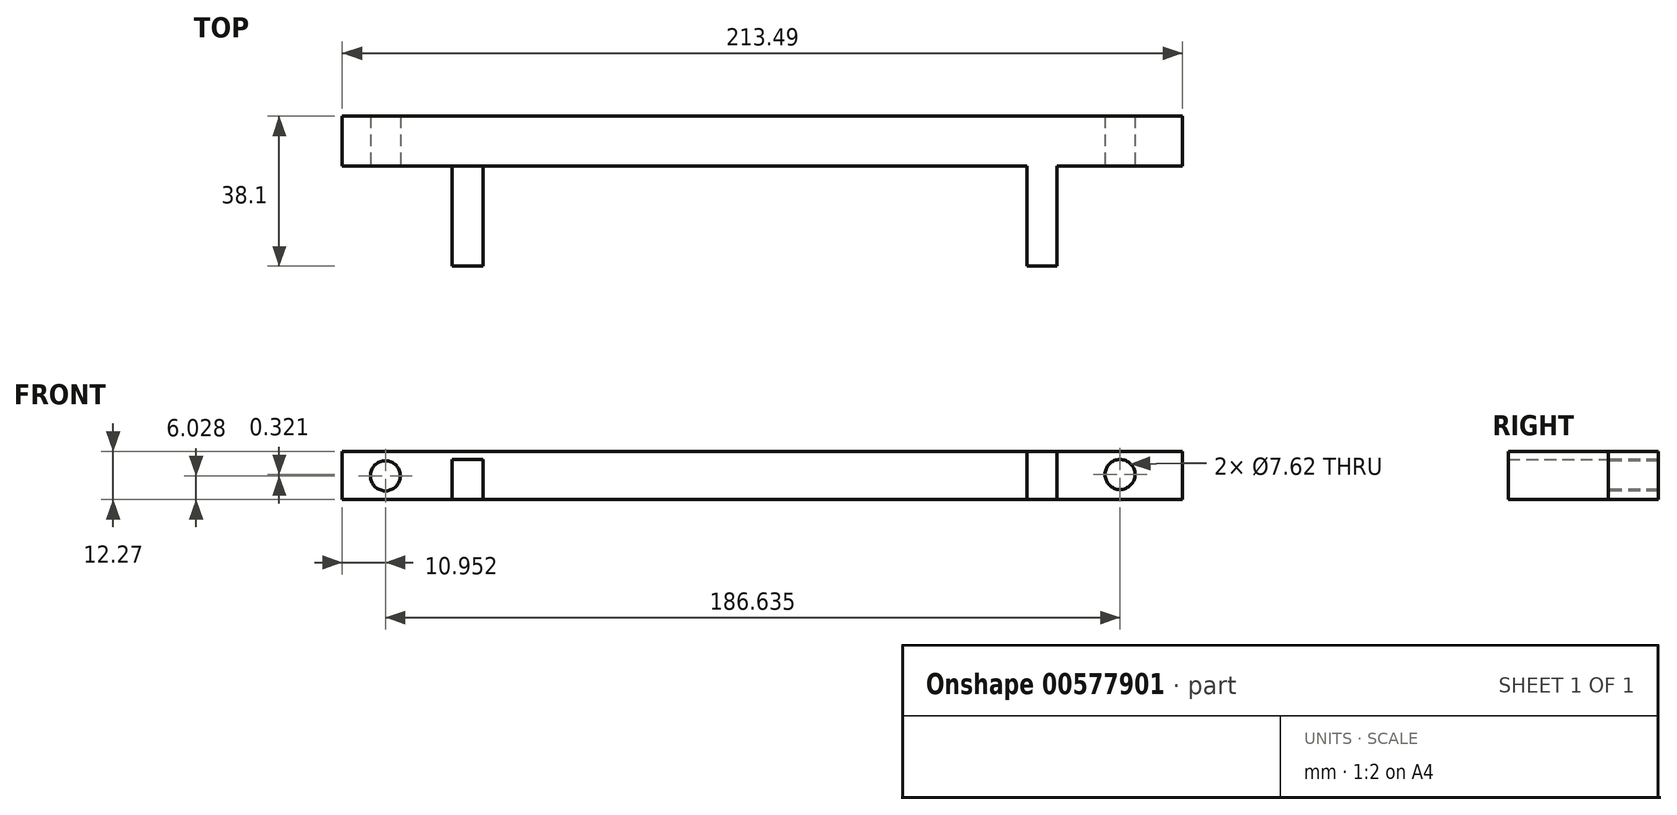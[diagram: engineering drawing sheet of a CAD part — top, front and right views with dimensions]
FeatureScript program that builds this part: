
annotation { "Feature Type Name" : "Feature", "Feature Type Description" : "" }
export const myFeature = defineFeature(function(context is Context, id is Id, definition is map)
    precondition{}
    {
        {
            var Q0;
            Q0=qCreatedBy(makeId("Front.planeOp"),FACE);
            var sketch = newSketch(context, id + "F0", { "sketchPlane" : qUnion([Q0])});
            skLineSegment(sketch, "E0.bottom", {"start": v(-75.05, 47.97) * mm, "end": v(138.44, 47.97) * mm});
            skLineSegment(sketch, "E0.top", {"start": v(-75.05, 35.7) * mm, "end": v(138.44, 35.7) * mm});
            skLineSegment(sketch, "E0.left", {"start": v(-75.05, 47.97) * mm, "end": v(-75.05, 35.7) * mm});
            skLineSegment(sketch, "E0.right", {"start": v(138.44, 47.97) * mm, "end": v(138.44, 35.7) * mm});
            skSolve(sketch);
        }
        {
            var Q0;
            Q0=makeQuery(id+"F0.imprint","IMPRINT",FACE,{"disambiguationData":[TD([[makeQuery(id+"F0.imprint","IMPRINT",EDGE,{"derivedFrom":sQuery(id+"F0.wireOp",EDGE,"E0.bottom")}),-1.0]])]});
            extrude(context, id + "F1", {"entities" : qUnion([Q0]), "depth" : 12.7 * mm, "offsetDistance" : 25.4 * mm});
        }
        {
            var Q0;
            Q0=makeQuery(id+"F1.opExtrude","CAP_FACE",FACE,{"disambiguationData":[OSD([sQuery(id+"F0.wireOp",EDGE,"E0.bottom"),sQuery(id+"F0.wireOp",EDGE,"E0.top"),sQuery(id+"F0.wireOp",EDGE,"E0.left"),sQuery(id+"F0.wireOp",EDGE,"E0.right")])],"isStart":false});
            var sketch = newSketch(context, id + "F2", { "sketchPlane" : qUnion([Q0])});
            skPoint(sketch, "E1", {"position": v(-63.84, 35.7) * mm});
            skPoint(sketch, "E2", {"position": v(-64.1, 41.73) * mm});
            skSolve(sketch);
        }
        {
            var Q0;
            Q0=sQuery(id+"F2.wireOp",VERTEX,"E2");
            var Q1;
            Q1=makeQuery(id+"F1.opExtrude","SWEPT_BODY",BODY,{"disambiguationData":[OSD([sQuery(id+"F0.wireOp",EDGE,"E0.bottom"),sQuery(id+"F0.wireOp",EDGE,"E0.top"),sQuery(id+"F0.wireOp",EDGE,"E0.left"),sQuery(id+"F0.wireOp",EDGE,"E0.right")])]});
            hole(context, id + "F3", {"style" : HoleStyle.SIMPLE, "endStyle" : HoleEndStyle.THROUGH, "holeDiameter" : 7.62 * mm, "isTappedThrough" : true, "tappedDepth" : 12.7 * mm, "tapClearance" : 3, "locations" : qUnion([Q0]), "scope" : qUnion([Q1])});
        }
        {
            var Q0;
            Q0=makeQuery(id+"F1.opExtrude","CAP_FACE",FACE,{"disambiguationData":[OSD([sQuery(id+"F0.wireOp",EDGE,"E0.bottom"),sQuery(id+"F0.wireOp",EDGE,"E0.top"),sQuery(id+"F0.wireOp",EDGE,"E0.left"),sQuery(id+"F0.wireOp",EDGE,"E0.right")])],"isStart":false});
            var sketch = newSketch(context, id + "F4", { "sketchPlane" : qUnion([Q0])});
            skPoint(sketch, "E3", {"position": v(122.54, 35.7) * mm});
            skPoint(sketch, "E4", {"position": v(122.54, 42.05) * mm});
            skSolve(sketch);
        }
        {
            var Q0;
            Q0=sQuery(id+"F4.wireOp",VERTEX,"E4");
            var Q1;
            Q1=makeQuery(id+"F1.opExtrude","SWEPT_BODY",BODY,{"disambiguationData":[OSD([sQuery(id+"F0.wireOp",EDGE,"E0.bottom"),sQuery(id+"F0.wireOp",EDGE,"E0.top"),sQuery(id+"F0.wireOp",EDGE,"E0.left"),sQuery(id+"F0.wireOp",EDGE,"E0.right")])]});
            hole(context, id + "F5", {"style" : HoleStyle.SIMPLE, "endStyle" : HoleEndStyle.THROUGH, "holeDiameter" : 7.62 * mm, "isTappedThrough" : true, "tappedDepth" : 12.7 * mm, "tapClearance" : 3, "locations" : qUnion([Q0]), "scope" : qUnion([Q1])});
        }
        {
            var Q0;
            Q0=qCreatedBy(makeId("Front.planeOp"),FACE);
            var sketch = newSketch(context, id + "F6", { "sketchPlane" : qUnion([Q0])});
            skLineSegment(sketch, "E5", {"start": v(-47.13, 45.94) * mm, "end": v(-47.13, 40.67) * mm});
            skLineSegment(sketch, "E6", {"start": v(-47.13, 40.67) * mm, "end": v(-39.24, 40.67) * mm});
            skLineSegment(sketch, "E7", {"start": v(-39.24, 40.67) * mm, "end": v(-39.24, 45.94) * mm});
            skLineSegment(sketch, "E8", {"start": v(-39.24, 45.94) * mm, "end": v(-47.13, 45.94) * mm});
            skSolve(sketch);
        }
        {
            var Q0;
            Q0=makeQuery(id+"F6.imprint","IMPRINT",FACE,{"disambiguationData":[TD([[makeQuery(id+"F6.imprint","IMPRINT",EDGE,{"derivedFrom":sQuery(id+"F6.wireOp",EDGE,"E5")}),1.0]])]});
            extrude(context, id + "F7", {"entities" : qUnion([Q0]), "operationType" : NewBodyOperationType.ADD, "depth" : 25.4 * mm, "offsetDistance" : 25.4 * mm});
        }
        {
            var Q0;
            Q0=makeQuery(id+"F1.opExtrude","CAP_FACE",FACE,{"disambiguationData":[OSD([sQuery(id+"F0.wireOp",EDGE,"E0.bottom"),sQuery(id+"F0.wireOp",EDGE,"E0.top"),sQuery(id+"F0.wireOp",EDGE,"E0.left"),sQuery(id+"F0.wireOp",EDGE,"E0.right")])],"isStart":false});
            var sketch = newSketch(context, id + "F8", { "sketchPlane" : qUnion([Q0])});
            skLineSegment(sketch, "E9", {"start": v(106.47, 35.7) * mm, "end": v(106.47, 47.97) * mm});
            skLineSegment(sketch, "E10", {"start": v(106.47, 47.97) * mm, "end": v(98.88, 47.97) * mm});
            skLineSegment(sketch, "E11", {"start": v(98.88, 47.97) * mm, "end": v(98.88, 35.7) * mm});
            skLineSegment(sketch, "E12", {"start": v(98.88, 35.7) * mm, "end": v(106.47, 35.7) * mm});
            skSolve(sketch);
        }
        {
            var Q0;
            Q0=makeQuery(id+"F8.imprint","IMPRINT",FACE,{"disambiguationData":[TD([[makeQuery(id+"F8.imprint","IMPRINT",EDGE,{"derivedFrom":sQuery(id+"F8.wireOp",EDGE,"E9")}),1.0]])]});
            extrude(context, id + "F9", {"entities" : qUnion([Q0]), "operationType" : NewBodyOperationType.ADD, "depth" : 25.4 * mm, "offsetDistance" : 25.4 * mm});
        }
        {
            var Q0;
            {var subQ0=sQuery(id+"F0.wireOp",EDGE,"E0.bottom");var subQ1=sQuery(id+"F0.wireOp",EDGE,"E0.top");var subQ2=sQuery(id+"F0.wireOp",EDGE,"E0.left");Q0=makeQuery(id+"F9.boolean.opBoolean","SPLIT",FACE,{"disambiguationData":[TD([makeQuery(id+"F1.opExtrude","SWEPT_FACE",FACE,{"disambiguationData":[OSD([subQ2])]})])],"derivedFrom":makeQuery(id+"F1.opExtrude","CAP_FACE",FACE,{"disambiguationData":[OSD([subQ0,subQ1,subQ2,sQuery(id+"F0.wireOp",EDGE,"E0.right")])],"isStart":false})});}
            var sketch = newSketch(context, id + "F10", { "sketchPlane" : qUnion([Q0])});
            skLineSegment(sketch, "E13", {"start": v(-47.13, 40.67) * mm, "end": v(-47.13, 35.7) * mm});
            skLineSegment(sketch, "E14", {"start": v(-47.13, 35.7) * mm, "end": v(-39.24, 35.7) * mm});
            skLineSegment(sketch, "E15", {"start": v(-39.24, 35.7) * mm, "end": v(-39.24, 40.67) * mm});
            skLineSegment(sketch, "E16", {"start": v(-39.24, 40.67) * mm, "end": v(-47.13, 40.67) * mm});
            skSolve(sketch);
        }
        {
            var Q0;
            Q0=makeQuery(id+"F10.imprint","IMPRINT",FACE,{"disambiguationData":[TD([[makeQuery(id+"F10.imprint","IMPRINT",EDGE,{"derivedFrom":sQuery(id+"F10.wireOp",EDGE,"E13")}),1.0]])]});
            extrude(context, id + "F11", {"entities" : qUnion([Q0]), "operationType" : NewBodyOperationType.ADD, "depth" : 25.4 * mm, "offsetDistance" : 25.4 * mm});
        }
        {
            var Q0;
            Q0=makeQuery(id+"F7.opExtrude","CAP_FACE",FACE,{"disambiguationData":[OSD([sQuery(id+"F6.wireOp",EDGE,"E5"),sQuery(id+"F6.wireOp",EDGE,"E6"),sQuery(id+"F6.wireOp",EDGE,"E7"),sQuery(id+"F6.wireOp",EDGE,"E8")])],"isStart":false});
            extrude(context, id + "F12", {"entities" : qUnion([Q0]), "operationType" : NewBodyOperationType.ADD, "depth" : 12.7 * mm, "offsetDistance" : 25.4 * mm});
        }
    });
